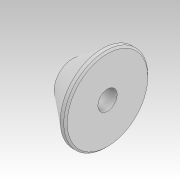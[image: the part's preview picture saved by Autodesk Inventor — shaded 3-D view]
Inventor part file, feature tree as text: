
AUTODESK INVENTOR PART (.ipt)
format: ipt  version: 2020 (Build 240168000, 168)  size: 99,328 bytes
history: native  units: mm
features: revolve x1, sketch x1
ambient origin geometry x8: Origin, YZ Plane, XZ Plane, XY Plane, X Axis, Y Axis, Z Axis, Center Point
bodies: Solid1 (feature_tree)
feature tree (2):
  revolve  "Revolution1"  [1 undecoded]
  sketch  "Sketch1"  dims[d0=2.75mm d1=10.0mm d2=2.5mm d3=1.5mm d4=12.0mm d5=0.5mm d6=0.5mm d7=90.0deg]
note: 1 required parameter value undecoded (feature->parameter linkage not recoverable at this tier; creation-order binding heuristic only, values carry confidence <= 0.55)
